# Revit family: ROTADO_Вентилятор_Разгонный_РВО D
name_source: partatom
category: Оборудование
units: mm (PartAtom-declared; Revit-internal decimal feet)

## family parameters
Всегда вертикально = Да
Классификация = Нет
На основе рабочей плоскости = Нет
Общий = Нет
При загрузке вырезать с полостями = Нет
Размер круглого соединителя = Использовать диаметр
Тип детали = Нормальный
Точка расчета площади = Нет

## types (6) — shared parameters
ADSK_URL документации изделия = https://rotado.ru
ADSK_URL страницы изделия = https://rotado.ru
ADSK_Версия Revit = 2019
ADSK_Единица измерения = шт.
ADSK_Завод-изготовитель = ROTADO
ADSK_Классификация нагрузок = Прочее
ADSK_Количество = 1
ADSK_Количество фаз = 3
ADSK_Количество фаз числовое = 3
ADSK_Коэффициент мощности = 1
ADSK_Материал = ROTADO_Сталь_Нержавеющая_Оцинкованная
ADSK_Наименование = Разгонные вентиляторы с прямым приводом
ADSK_Напряжение = 380 В
ADSK_Размер_Длина = 410 мм
G = 410 мм
URL = https://rotado.ru
d1 = 160 мм
Изготовитель = ROTADO
Логотип_Видимость = Да
Производитель_Контакты_Телефон = 88007002460

## per-type parameters (varying)
| type | A | ADSK_Марка | ADSK_Масса | ADSK_Масса_Текст | ADSK_Номинальная мощность | ADSK_Обозначение | ADSK_Полная мощность | ADSK_Размер_Высота | ADSK_Размер_Диаметр | ADSK_Размер_Ширина | A_1 | D | k |
| Вентилятор_Разгонный_ РВО(D)-1000 | 1150 мм | РВО(D)-1000-Combo430 | 40 | 40 кг | 370 Вт | РВО(D)-1000-Combo430 | 370 В·А | 1150 мм | 1000 мм | 1150 мм | 1200 мм | 1000 мм | 12 мм |
| Вентилятор_Разгонный_РВО(D)-1000-Combo304 | 1150 мм | РВО(D)-1000-Combo304 | 40 | 40 кг | 370 Вт | РВО(D)-1000-Combo304 | 370 В·А | 1150 мм | 1000 мм | 1150 мм | 1200 мм | 1000 мм | 12 мм |
| Вентилятор_Разгонный_РВО(D)-1000-Combo430 | 1150 мм | РВО(D)-1000-Combo430 | 40 | 40 кг | 370 Вт | РВО(D)-1000-Combo430 | 370 В·А | 1150 мм | 1000 мм | 1150 мм | 1200 мм | 1000 мм | 12 мм |
| Вентилятор_Разгонный_РВО-(D)-1200 | 1400 мм | РВО-(D)-1200 | 46 | 46 кг | 550 Вт | РВО-(D)-1200 | 550 В·А | 1400 мм | 1200 мм | 1400 мм | 1450 мм | 1200 мм | 15 мм |
| Вентилятор_Разгонный_РВО-(D)-1200-Combo304 | 1400 мм | РВО-(D)-1200-Combo304 | 46 | 46 кг | 550 Вт | РВО-(D)-1200-Combo304 | 550 В·А | 1400 мм | 1200 мм | 1400 мм | 1450 мм | 1200 мм | 15 мм |
| Вентилятор_Разгонный_РВО-(D)-1200-Combo430 | 1400 мм | РВО-(D)-1200-Combo430 | 46 | 46 кг | 550 Вт | РВО-(D)-1200-Combo430 | 550 В·А | 1400 мм | 1200 мм | 1400 мм | 1450 мм | 1200 мм | 15 мм |
